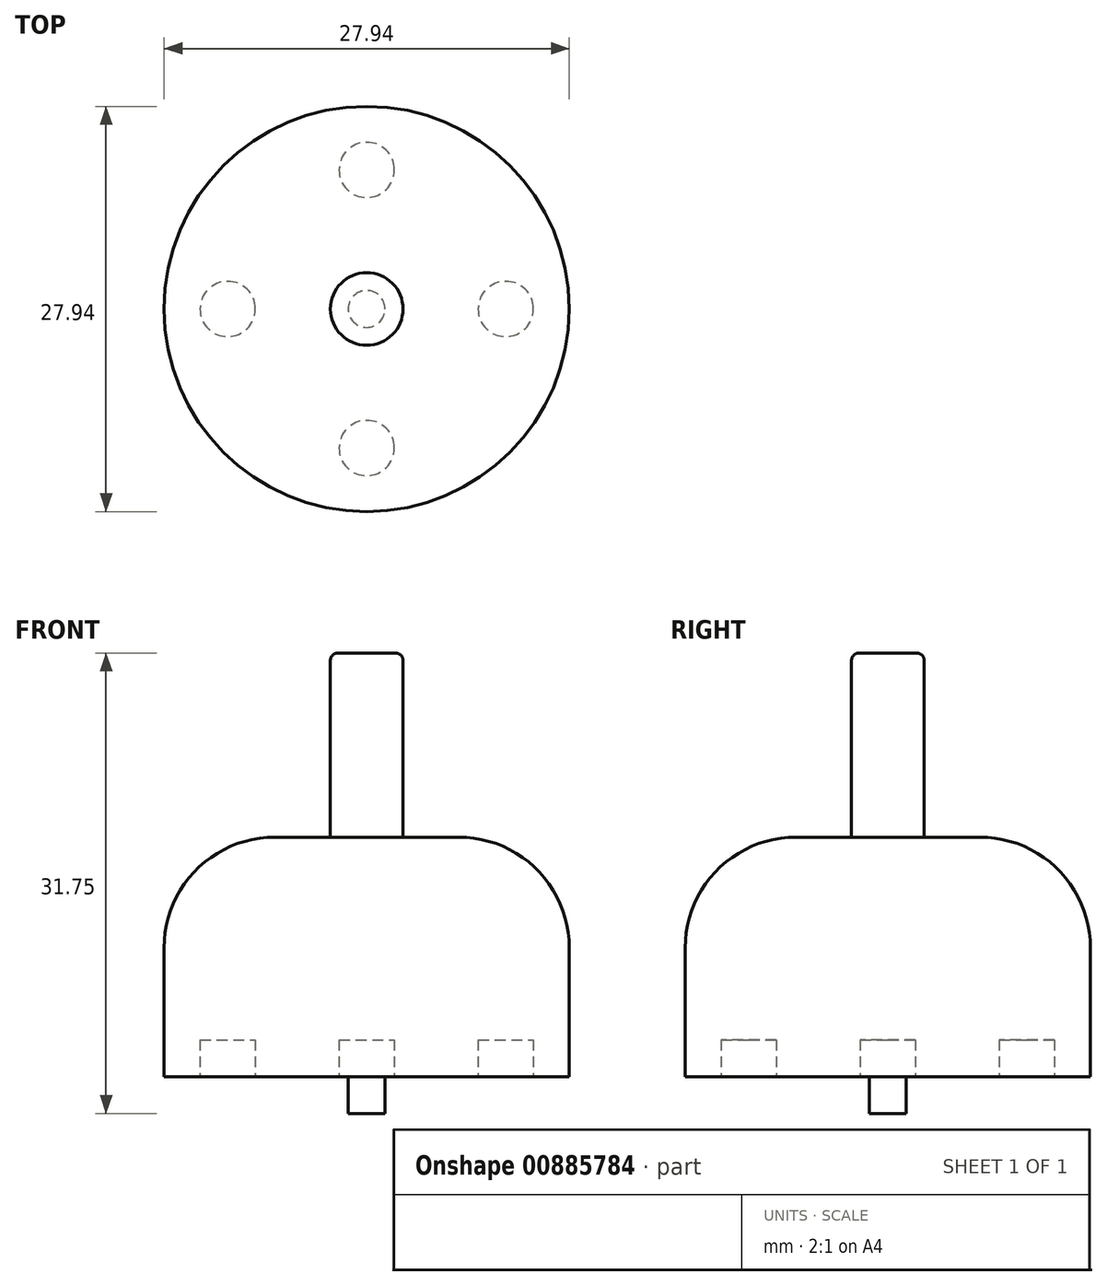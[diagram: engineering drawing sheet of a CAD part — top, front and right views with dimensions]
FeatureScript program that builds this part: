
annotation { "Feature Type Name" : "Feature", "Feature Type Description" : "" }
export const myFeature = defineFeature(function(context is Context, id is Id, definition is map)
    precondition{}
    {
        {
            var Q0;
            Q0=qCreatedBy(makeId("Top.planeOp"),FACE);
            var sketch = newSketch(context, id + "F0", { "sketchPlane" : qUnion([Q0])});
            skCircle(sketch, "E0", {"center": v(0, 0) * mm, "radius": 13.97 * mm});
            skSolve(sketch);
        }
        {
            var Q0;
            Q0 = qSketchRegion(id + "F0", true);
            extrude(context, id + "F1", {"entities" : qUnion([Q0]), "depth" : 16.5 * mm, "offsetDistance" : 25.4 * mm});
        }
        {
            var Q0;
            Q0=makeQuery(id+"F1.opExtrude","CAP_EDGE",EDGE,{"disambiguationData":[OSD([sQuery(id+"F0.wireOp",EDGE,"E0")])],"isStart":false});
            fillet(context, id + "F2", {"entities" : qUnion([Q0]), "radius" : 7.62 * mm, "tangentPropagation" : true, "allowEdgeOverflow" : false});
        }
        {
            var Q0;
            Q0=makeQuery(id+"F1.opExtrude","CAP_FACE",FACE,{"disambiguationData":[OSD([sQuery(id+"F0.wireOp",EDGE,"E0")])],"isStart":true});
            var sketch = newSketch(context, id + "F3", { "sketchPlane" : qUnion([Q0])});
            skCircle(sketch, "E1", {"center": v(0, 0) * mm, "radius": 1.27 * mm});
            skSolve(sketch);
        }
        {
            var Q0;
            Q0=makeQuery(id+"F3.imprint","IMPRINT",FACE,{"disambiguationData":[TD([[makeQuery(id+"F3.imprint","IMPRINT",EDGE,{"derivedFrom":sQuery(id+"F3.wireOp",EDGE,"E1")}),1.0]])]});
            extrude(context, id + "F4", {"entities" : qUnion([Q0]), "operationType" : NewBodyOperationType.ADD, "depth" : 2.54 * mm, "offsetDistance" : 25.4 * mm});
        }
        {
            var Q0;
            Q0=makeQuery(id+"F1.opExtrude","CAP_FACE",FACE,{"disambiguationData":[OSD([sQuery(id+"F0.wireOp",EDGE,"E0")])],"isStart":true});
            var sketch = newSketch(context, id + "F5", { "sketchPlane" : qUnion([Q0])});
            skLineSegment(sketch, "E2", {"start": v(0, 0) * mm, "end": v(0, -9.59) * mm, "construction": true});
            skCircle(sketch, "E3", {"center": v(0, -9.59) * mm, "radius": 1.9 * mm});
            skCircle(sketch, "E4.1.0", {"center": v(9.59, 0) * mm, "radius": 1.9 * mm});
            skCircle(sketch, "E4.2.0", {"center": v(0, 9.59) * mm, "radius": 1.9 * mm});
            skCircle(sketch, "E4.3.0", {"center": v(-9.59, 0) * mm, "radius": 1.9 * mm});
            skPoint(sketch, "E4.center", {"position": v(0, 0) * mm});
            skSolve(sketch);
        }
        {
            var Q0;
            Q0=makeQuery(id+"F5.imprint","IMPRINT",FACE,{"disambiguationData":[TD([[makeQuery(id+"F5.imprint","IMPRINT",EDGE,{"derivedFrom":sQuery(id+"F5.wireOp",EDGE,"E4.3.0")}),1.0]])]});
            var Q1;
            Q1=makeQuery(id+"F5.imprint","IMPRINT",FACE,{"disambiguationData":[TD([[makeQuery(id+"F5.imprint","IMPRINT",EDGE,{"derivedFrom":sQuery(id+"F5.wireOp",EDGE,"E3")}),1.0]])]});
            var Q2;
            Q2=makeQuery(id+"F5.imprint","IMPRINT",FACE,{"disambiguationData":[TD([[makeQuery(id+"F5.imprint","IMPRINT",EDGE,{"derivedFrom":sQuery(id+"F5.wireOp",EDGE,"E4.1.0")}),1.0]])]});
            var Q3;
            Q3=makeQuery(id+"F5.imprint","IMPRINT",FACE,{"disambiguationData":[TD([[makeQuery(id+"F5.imprint","IMPRINT",EDGE,{"derivedFrom":sQuery(id+"F5.wireOp",EDGE,"E4.2.0")}),1.0]])]});
            extrude(context, id + "F6", {"entities" : qUnion([Q0, Q1, Q2, Q3]), "operationType" : NewBodyOperationType.REMOVE, "oppositeDirection" : true, "depth" : 2.54 * mm, "offsetDistance" : 25.4 * mm});
        }
        {
            var Q0;
            Q0=makeQuery(id+"F1.opExtrude","CAP_FACE",FACE,{"disambiguationData":[OSD([sQuery(id+"F0.wireOp",EDGE,"E0")])],"isStart":false});
            var sketch = newSketch(context, id + "F7", { "sketchPlane" : qUnion([Q0])});
            skCircle(sketch, "E5", {"center": v(0, 0) * mm, "radius": 2.5 * mm});
            skSolve(sketch);
        }
        {
            var Q0;
            Q0=makeQuery(id+"F7.imprint","IMPRINT",FACE,{"disambiguationData":[TD([[makeQuery(id+"F7.imprint","IMPRINT",EDGE,{"derivedFrom":sQuery(id+"F7.wireOp",EDGE,"E5")}),1.0]])]});
            extrude(context, id + "F8", {"entities" : qUnion([Q0]), "operationType" : NewBodyOperationType.ADD, "depth" : 12.7 * mm, "offsetDistance" : 25.4 * mm});
        }
        {
            var Q0;
            Q0=makeQuery(id+"F8.opExtrude","CAP_EDGE",EDGE,{"disambiguationData":[OSD([sQuery(id+"F7.wireOp",EDGE,"E5")])],"isStart":false});
            fillet(context, id + "F9", {"entities" : qUnion([Q0]), "radius" : 0.5 * mm, "tangentPropagation" : true, "allowEdgeOverflow" : false});
        }
    });
